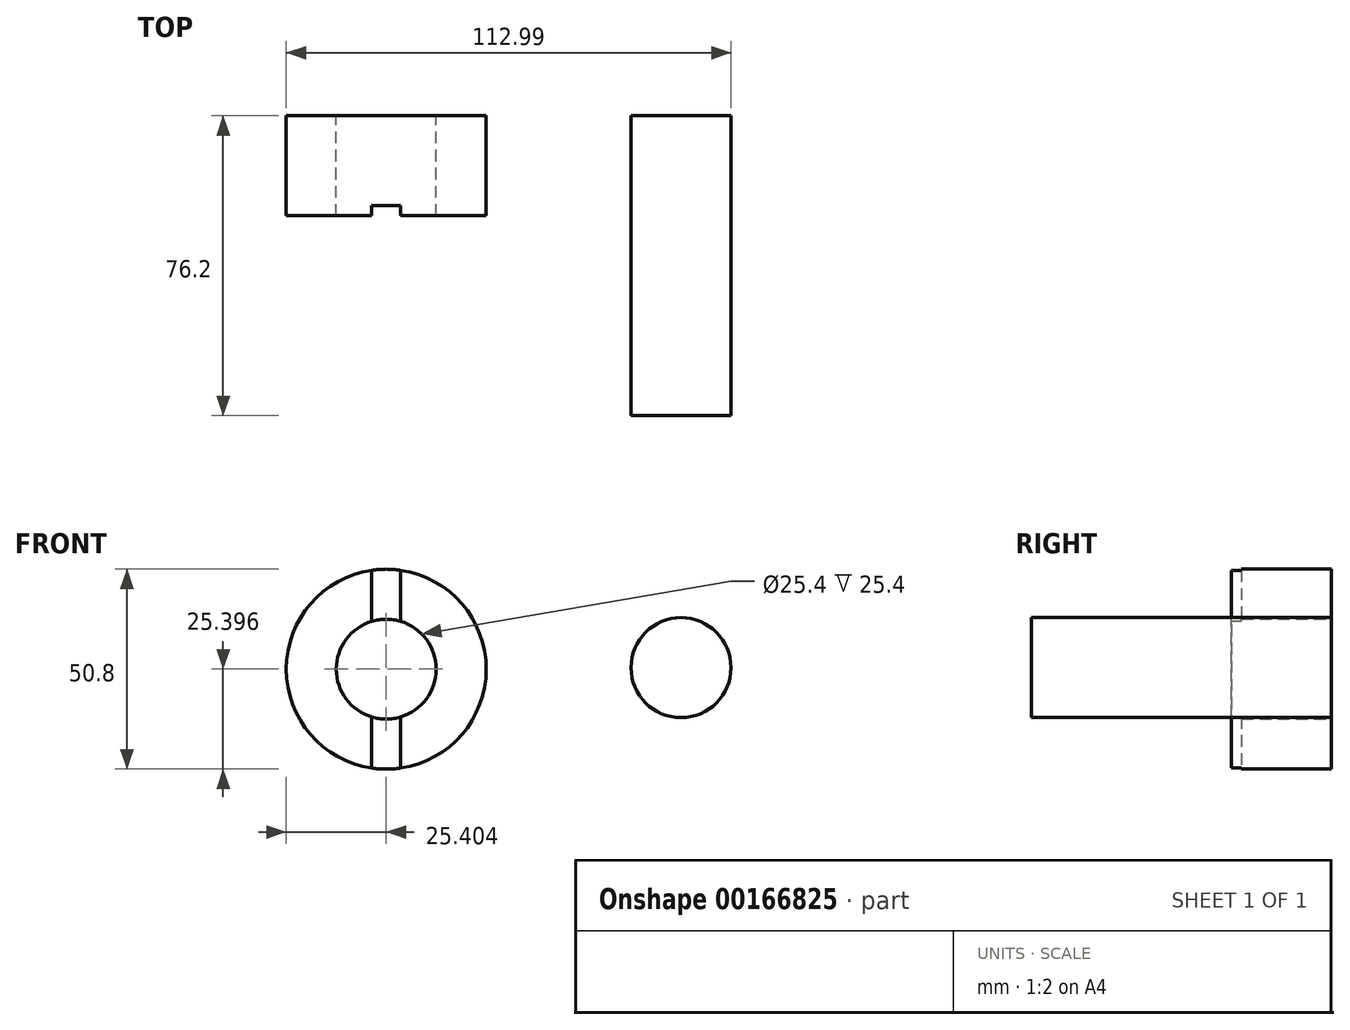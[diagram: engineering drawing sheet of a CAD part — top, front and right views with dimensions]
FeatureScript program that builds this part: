
annotation { "Feature Type Name" : "Feature", "Feature Type Description" : "" }
export const myFeature = defineFeature(function(context is Context, id is Id, definition is map)
    precondition{}
    {
        {
            var Q0;
            Q0=qCreatedBy(makeId("Front.planeOp"),FACE);
            var sketch = newSketch(context, id + "F0", { "sketchPlane" : qUnion([Q0])});
            skCircle(sketch, "E0", {"center": v(-42.96, 31.06) * mm, "radius": 12.7 * mm});
            skCircle(sketch, "E1", {"center": v(-42.96, 31.06) * mm, "radius": 25.4 * mm});
            skSolve(sketch);
        }
        {
            var Q0;
            Q0=qCreatedBy(makeId("Front.planeOp"),FACE);
            var sketch = newSketch(context, id + "F1", { "sketchPlane" : qUnion([Q0])});
            skCircle(sketch, "E2", {"center": v(31.93, 31.44) * mm, "radius": 12.7 * mm});
            skSolve(sketch);
        }
        {
            var Q0;
            Q0=makeQuery(id+"F1.imprint","IMPRINT",FACE,{"disambiguationData":[TD([[makeQuery(id+"F1.imprint","IMPRINT",EDGE,{"derivedFrom":sQuery(id+"F1.wireOp",EDGE,"E2")}),1.0]])]});
            extrude(context, id + "F2", {"entities" : qUnion([Q0]), "depth" : 76.2 * mm});
        }
        {
            var Q0;
            Q0=makeQuery(id+"F0.imprint","IMPRINT",FACE,{"disambiguationData":[TD([[makeQuery(id+"F0.imprint","IMPRINT",EDGE,{"derivedFrom":sQuery(id+"F0.wireOp",EDGE,"E0")}),-1.0]])]});
            extrude(context, id + "F3", {"entities" : qUnion([Q0]), "depth" : 25.4 * mm});
        }
        {
            var Q0;
            Q0=makeQuery(id+"F3.opExtrude","CAP_FACE",FACE,{"disambiguationData":[OSD([sQuery(id+"F0.wireOp",EDGE,"E0"),sQuery(id+"F0.wireOp",EDGE,"E1")])],"isStart":false});
            var sketch = newSketch(context, id + "F4", { "sketchPlane" : qUnion([Q0])});
            skLineSegment(sketch, "E3.bottom", {"start": v(-46.63, 60.47) * mm, "end": v(-39.28, 60.47) * mm});
            skLineSegment(sketch, "E3.top", {"start": v(-46.63, -6.1) * mm, "end": v(-39.28, -6.1) * mm});
            skLineSegment(sketch, "E3.left", {"start": v(-46.63, 60.47) * mm, "end": v(-46.63, -6.1) * mm});
            skLineSegment(sketch, "E3.right", {"start": v(-39.28, 60.47) * mm, "end": v(-39.28, -6.1) * mm});
            skSolve(sketch);
        }
        {
            var Q0;
            {var subQ0=sQuery(id+"F4.wireOp",EDGE,"E3.left");var subQ1=makeQuery(id+"F3.opExtrude","CAP_EDGE",EDGE,{"disambiguationData":[OSD([sQuery(id+"F0.wireOp",EDGE,"E1")])],"isStart":false});var subQ2=makeQuery(id+"F4.imprint","INTERSECT",VERTEX,{"disambiguationData":[OD(0.0)],"derivedFrom":[subQ1,subQ0]});Q0=makeQuery(id+"F4.imprint","IMPRINT",FACE,{"disambiguationData":[TD([[makeQuery(id+"F4.imprint","IMPRINT",EDGE,{"disambiguationData":[TD([[subQ2,-1.0]])],"derivedFrom":subQ0}),1.0]])]});}
            var Q1;
            {var subQ0=sQuery(id+"F4.wireOp",EDGE,"E3.left");var subQ1=makeQuery(id+"F3.opExtrude","CAP_EDGE",EDGE,{"disambiguationData":[OSD([sQuery(id+"F0.wireOp",EDGE,"E1")])],"isStart":false});var subQ2=makeQuery(id+"F4.imprint","INTERSECT",VERTEX,{"disambiguationData":[OD(1.0)],"derivedFrom":[subQ1,subQ0]});Q1=makeQuery(id+"F4.imprint","IMPRINT",FACE,{"disambiguationData":[TD([[makeQuery(id+"F4.imprint","IMPRINT",EDGE,{"disambiguationData":[TD([[subQ2,1.0]])],"derivedFrom":subQ0}),1.0]])]});}
            extrude(context, id + "F5", {"entities" : qUnion([Q0, Q1]), "operationType" : NewBodyOperationType.REMOVE, "oppositeDirection" : true, "depth" : 2.54 * mm});
        }
    });
